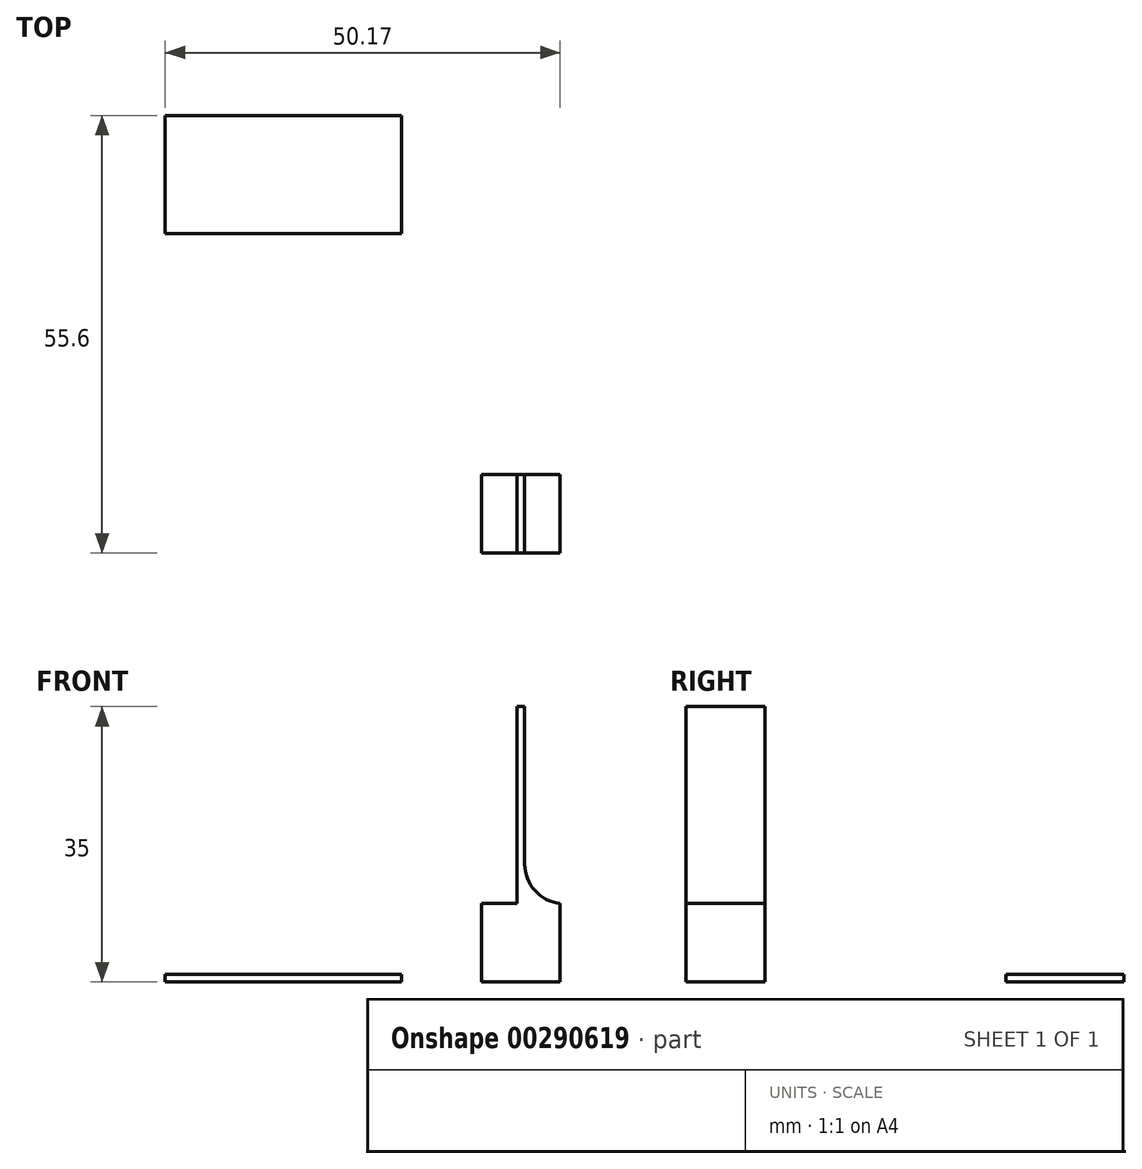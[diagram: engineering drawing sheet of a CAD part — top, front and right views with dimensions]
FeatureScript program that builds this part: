
annotation { "Feature Type Name" : "Feature", "Feature Type Description" : "" }
export const myFeature = defineFeature(function(context is Context, id is Id, definition is map)
    precondition{}
    {
        {
            var Q0;
            Q0=qCreatedBy(makeId("Top.planeOp"),FACE);
            var sketch = newSketch(context, id + "F0", { "sketchPlane" : qUnion([Q0])});
            skLineSegment(sketch, "E0.bottom", {"start": v(-44.49, 49.7) * mm, "end": v(-14.49, 49.7) * mm});
            skLineSegment(sketch, "E0.top", {"start": v(-44.49, 34.7) * mm, "end": v(-14.49, 34.7) * mm});
            skLineSegment(sketch, "E0.left", {"start": v(-44.49, 49.7) * mm, "end": v(-44.49, 34.7) * mm});
            skLineSegment(sketch, "E0.right", {"start": v(-14.49, 49.7) * mm, "end": v(-14.49, 34.7) * mm});
            skSolve(sketch);
        }
        {
            var Q0;
            Q0 = qSketchRegion(id + "F0", true);
            extrude(context, id + "F1", {"entities" : qUnion([Q0]), "depth" : 1 * mm});
        }
        {
            var Q0;
            Q0=qCreatedBy(makeId("Top.planeOp"),FACE);
            var sketch = newSketch(context, id + "F2", { "sketchPlane" : qUnion([Q0])});
            skLineSegment(sketch, "E1.bottom", {"start": v(-4.32, 4.1) * mm, "end": v(5.68, 4.1) * mm});
            skLineSegment(sketch, "E1.top", {"start": v(-4.32, -5.9) * mm, "end": v(5.68, -5.9) * mm});
            skLineSegment(sketch, "E1.left", {"start": v(-4.32, 4.1) * mm, "end": v(-4.32, -5.9) * mm});
            skLineSegment(sketch, "E1.right", {"start": v(5.68, 4.1) * mm, "end": v(5.68, -5.9) * mm});
            skSolve(sketch);
        }
        {
            var Q0;
            Q0 = qSketchRegion(id + "F2", true);
            extrude(context, id + "F3", {"entities" : qUnion([Q0]), "depth" : 10 * mm});
        }
        {
            var Q0;
            Q0=makeQuery(id+"F3.opExtrude","CAP_FACE",FACE,{"disambiguationData":[OSD([sQuery(id+"F2.wireOp",EDGE,"E1.bottom"),sQuery(id+"F2.wireOp",EDGE,"E1.top"),sQuery(id+"F2.wireOp",EDGE,"E1.left"),sQuery(id+"F2.wireOp",EDGE,"E1.right")])],"isStart":false});
            var sketch = newSketch(context, id + "F4", { "sketchPlane" : qUnion([Q0])});
            skLineSegment(sketch, "E2", {"start": v(0.68, 4.1) * mm, "end": v(0.68, -5.9) * mm});
            skLineSegment(sketch, "E3", {"start": v(1.18, 4.1) * mm, "end": v(1.18, -5.9) * mm});
            skLineSegment(sketch, "E4", {"start": v(0.18, 4.1) * mm, "end": v(0.18, -5.9) * mm});
            skSolve(sketch);
        }
        {
            var Q0;
            {var subQ0=sQuery(id+"F4.wireOp",EDGE,"E2");Q0=makeQuery(id+"F4.imprint","IMPRINT",FACE,{"disambiguationData":[TD([[makeQuery(id+"F4.imprint","IMPRINT",EDGE,{"derivedFrom":subQ0}),-1.0]])]});}
            var Q1;
            {var subQ0=sQuery(id+"F4.wireOp",EDGE,"E2");Q1=makeQuery(id+"F4.imprint","IMPRINT",FACE,{"disambiguationData":[TD([[makeQuery(id+"F4.imprint","IMPRINT",EDGE,{"derivedFrom":subQ0}),1.0]])]});}
            extrude(context, id + "F5", {"entities" : qUnion([Q0, Q1]), "operationType" : NewBodyOperationType.ADD, "depth" : 25 * mm});
        }
        {
            var Q0;
            Q0=makeQuery(id+"F5.opExtrude","CAP_EDGE",EDGE,{"disambiguationData":[OSD([sQuery(id+"F4.wireOp",EDGE,"E4")])],"isStart":true});
            var Q1;
            Q1=makeQuery(id+"F5.opExtrude","CAP_EDGE",EDGE,{"disambiguationData":[OSD([sQuery(id+"F4.wireOp",EDGE,"E3")])],"isStart":true});
            fillet(context, id + "F6", {"entities" : qUnion([Q0, Q1]), "radius" : 5 * mm, "tangentPropagation" : true, "allowEdgeOverflow" : false});
        }
    });
